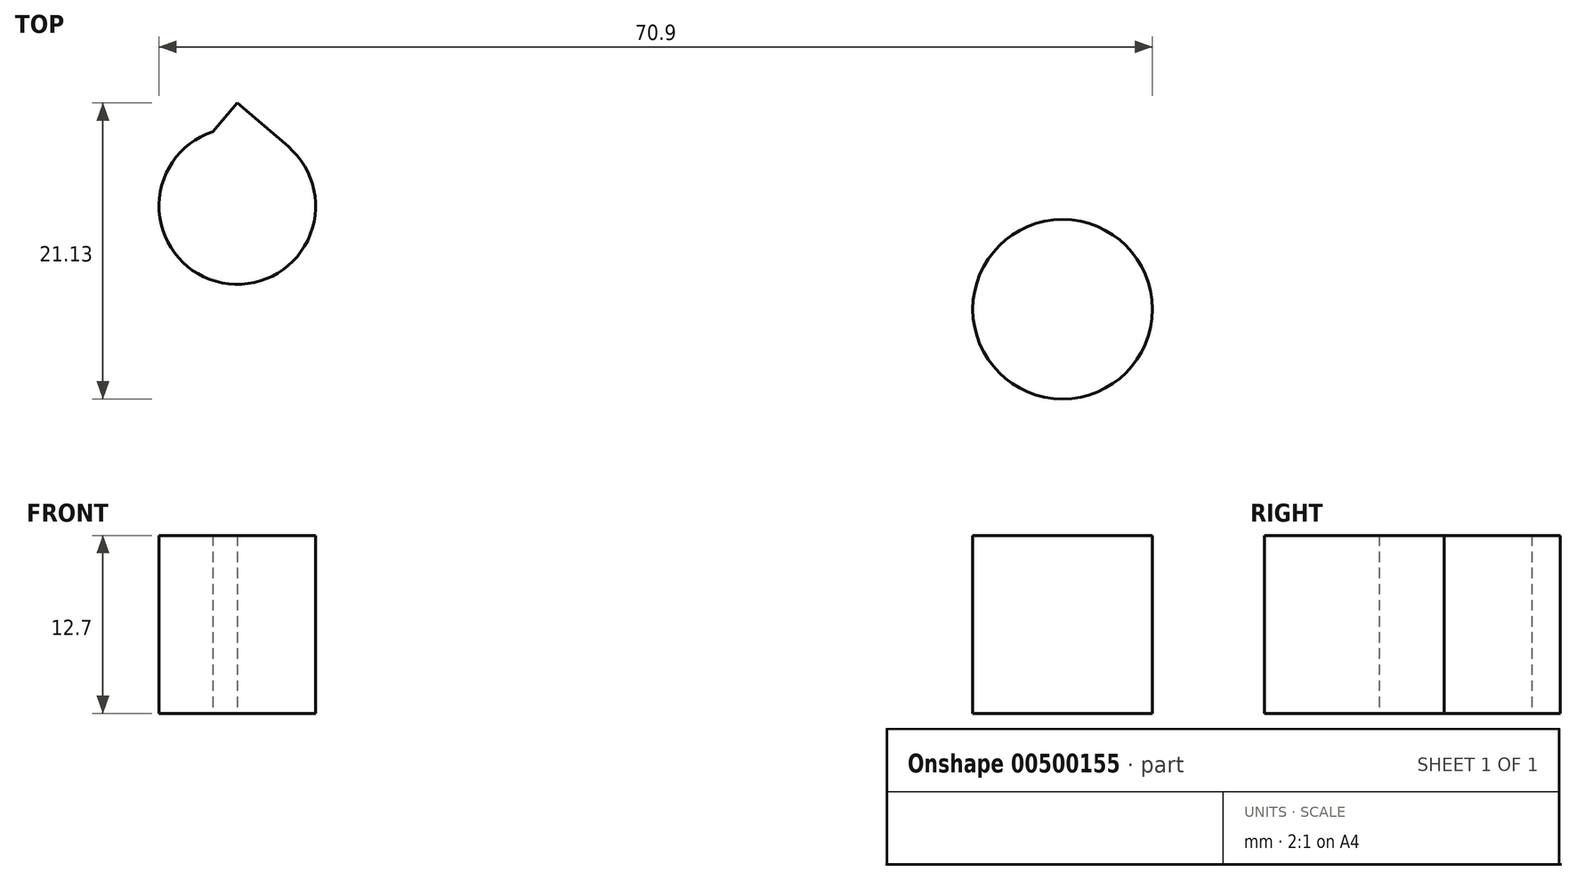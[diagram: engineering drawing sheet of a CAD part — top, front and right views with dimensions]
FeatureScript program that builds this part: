
annotation { "Feature Type Name" : "Feature", "Feature Type Description" : "" }
export const myFeature = defineFeature(function(context is Context, id is Id, definition is map)
    precondition{}
    {
        {
            var Q0;
            Q0=qCreatedBy(makeId("Top.planeOp"),FACE);
            var sketch = newSketch(context, id + "F0", { "sketchPlane" : qUnion([Q0])});
            skLineSegment(sketch, "E0", {"start": v(63.5, -31.9) * mm, "end": v(18.71, -31.9) * mm});
            skLineSegment(sketch, "E1", {"start": v(18.71, -31.9) * mm, "end": v(6.44, -17.18) * mm});
            skLineSegment(sketch, "E2", {"start": v(6.44, -17.18) * mm, "end": v(-5.22, -31.9) * mm});
            skLineSegment(sketch, "E3", {"start": v(-35.28, -31.9) * mm, "end": v(-5.22, -31.9) * mm});
            skLineSegment(sketch, "E4", {"start": v(-35.28, -31.9) * mm, "end": v(-52.46, -17.18) * mm});
            skLineSegment(sketch, "E5", {"start": v(-52.46, -17.18) * mm, "end": v(-65.08, -31.9) * mm});
            skLineSegment(sketch, "E6", {"start": v(-95.4, -31.9) * mm, "end": v(-65.08, -31.9) * mm});
            skLineSegment(sketch, "E7", {"start": v(-95.4, -31.9) * mm, "end": v(-95.4, 33.13) * mm});
            skLineSegment(sketch, "E8", {"start": v(-95.4, 33.13) * mm, "end": v(18.71, 33.13) * mm});
            skLineSegment(sketch, "E9", {"start": v(18.71, 33.13) * mm, "end": v(57.37, 0) * mm});
            skLineSegment(sketch, "E10", {"start": v(57.37, 0) * mm, "end": v(63.5, -27) * mm});
            skCircle(sketch, "E11", {"center": v(6.44, -31.9) * mm, "radius": 6.4 * mm});
            skCircle(sketch, "E12", {"center": v(-52.46, -24.54) * mm, "radius": 5.6 * mm});
            skPoint(sketch, "E12.centerSnap0", {"position": v(-58.77, -24.54) * mm});
            skSolve(sketch);
        }
        {
            var Q0;
            Q0 = qSketchRegion(id + "F0", true);
            extrude(context, id + "F1", {"entities" : qUnion([Q0]), "depth" : 12.7 * mm});
        }
    });
